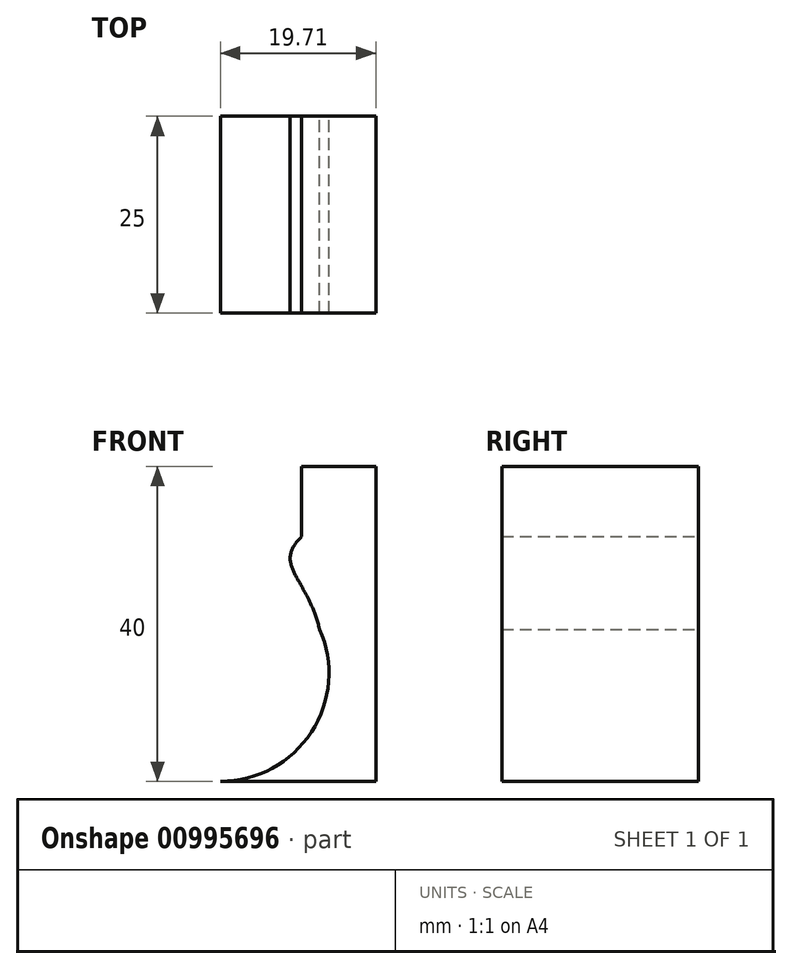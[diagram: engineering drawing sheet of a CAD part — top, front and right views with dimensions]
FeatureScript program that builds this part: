
annotation { "Feature Type Name" : "Feature", "Feature Type Description" : "" }
export const myFeature = defineFeature(function(context is Context, id is Id, definition is map)
    precondition{}
    {
        {
            var Q0;
            Q0=qCreatedBy(makeId("Front.planeOp"),FACE);
            var sketch = newSketch(context, id + "F0", { "sketchPlane" : qUnion([Q0])});
            skArc(sketch, "E0", {"start": v(21.1, -11.5) * mm, "mid": v(34.85, 2.26) * mm, "end": v(21.1, 16) * mm});
            skLineSegment(sketch, "E1", {"start": v(-54.06, 24.64) * mm, "end": v(-54.06, -20.26) * mm});
            skLineSegment(sketch, "E2", {"start": v(-54.06, -20.26) * mm, "end": v(-17.82, -20.26) * mm});
            skLineSegment(sketch, "E3", {"start": v(21.1, 16) * mm, "end": v(21.1, -11.5) * mm});
            skLineSegment(sketch, "E4", {"start": v(21.1, 11.83) * mm, "end": v(32.17, 11.83) * mm});
            skLineSegment(sketch, "E5", {"start": v(21.1, 28.5) * mm, "end": v(21.1, 11.83) * mm});
            skLineSegment(sketch, "E6", {"start": v(40.81, -11.5) * mm, "end": v(40.81, 28.5) * mm});
            skLineSegment(sketch, "E7", {"start": v(34.85, 2.26) * mm, "end": v(21.1, 2.26) * mm});
            skLineSegment(sketch, "E8", {"start": v(40.81, -11.5) * mm, "end": v(21.1, -11.5) * mm});
            skLineSegment(sketch, "E9", {"start": v(31.4, 28.5) * mm, "end": v(31.4, 19.61) * mm});
            skLineSegment(sketch, "E10", {"start": v(40.81, 28.5) * mm, "end": v(21.1, 28.5) * mm});
            skLineSegment(sketch, "E11", {"start": v(21.1, 16) * mm, "end": v(30.05, 16) * mm});
            skFitSpline(sketch, "E12", {"points": [v(33.67, 7.83) * mm, v(31.4, 19.61) * mm], "startDerivative": vector(-4.92, 20.08) * mm, "endDerivative": vector(11.2, 11.07) * mm});
            skSolve(sketch);
        }
        {
            var Q0;
            {var subQ5=sQuery(id+"F0.wireOp",EDGE,"E6");Q0=makeQuery(id+"F0.imprint","IMPRINT",FACE,{"disambiguationData":[TD([[makeQuery(id+"F0.imprint","IMPRINT",EDGE,{"derivedFrom":subQ5}),1.0]])]});}
            extrude(context, id + "F1", {"entities" : qUnion([Q0]), "depth" : 25 * mm, "offsetDistance" : 25 * mm});
        }
    });
